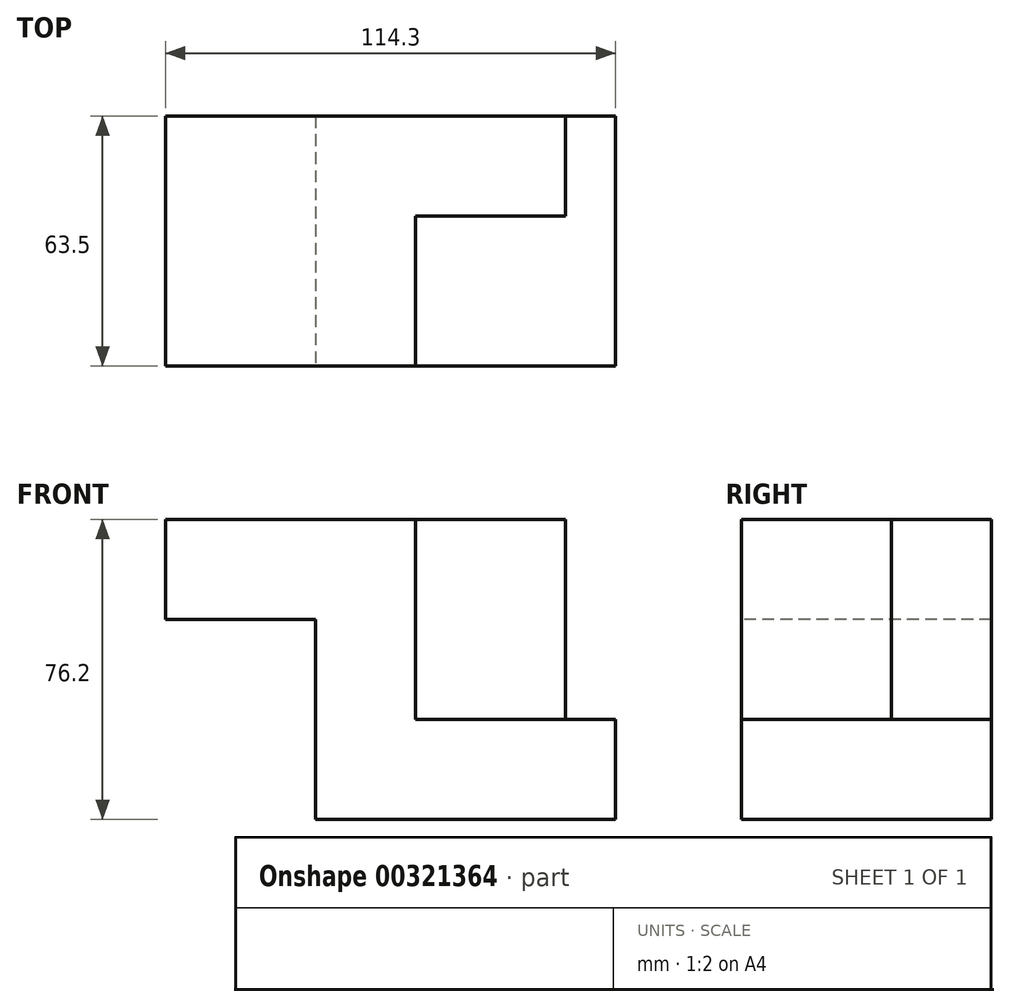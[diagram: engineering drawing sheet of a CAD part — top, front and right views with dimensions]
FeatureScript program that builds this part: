
annotation { "Feature Type Name" : "Feature", "Feature Type Description" : "" }
export const myFeature = defineFeature(function(context is Context, id is Id, definition is map)
    precondition{}
    {
        {
            var Q0;
            Q0=qCreatedBy(makeId("Front.planeOp"),FACE);
            var sketch = newSketch(context, id + "F0", { "sketchPlane" : qUnion([Q0])});
            skLineSegment(sketch, "E0", {"start": v(-34.58, -2.54) * mm, "end": v(-34.58, -27.94) * mm});
            skLineSegment(sketch, "E1", {"start": v(-34.58, -27.94) * mm, "end": v(41.62, -27.94) * mm});
            skLineSegment(sketch, "E2", {"start": v(41.62, -27.94) * mm, "end": v(41.62, -2.54) * mm});
            skLineSegment(sketch, "E3", {"start": v(41.62, -2.54) * mm, "end": v(-34.58, -2.54) * mm});
            skSolve(sketch);
        }
        {
            var Q0;
            Q0 = qSketchRegion(id + "F0", true);
            var Q1;
            Q1=makeQuery(id+"F0.imprint","IMPRINT",FACE,{"disambiguationData":[TD([[makeQuery(id+"F0.imprint","IMPRINT",EDGE,{"derivedFrom":sQuery(id+"F0.wireOp",EDGE,"E0")}),1.0]])]});
            extrude(context, id + "F1", {"entities" : qUnion([Q0, Q1]), "depth" : 63.5 * mm});
        }
        {
            var Q0;
            Q0=makeQuery(id+"F1.opExtrude","SWEPT_FACE",FACE,{"disambiguationData":[OSD([sQuery(id+"F0.wireOp",EDGE,"E3")])]});
            var sketch = newSketch(context, id + "F2", { "sketchPlane" : qUnion([Q0])});
            skLineSegment(sketch, "E4", {"start": v(-9.18, -63.5) * mm, "end": v(-9.18, -25.4) * mm});
            skLineSegment(sketch, "E5", {"start": v(-9.18, -25.4) * mm, "end": v(28.92, -25.4) * mm});
            skLineSegment(sketch, "E6", {"start": v(28.92, -25.4) * mm, "end": v(28.92, 0) * mm});
            skSolve(sketch);
        }
        {
            var Q0;
            {var subQ3=sQuery(id+"F2.wireOp",EDGE,"E4");Q0=makeQuery(id+"F2.imprint","IMPRINT",FACE,{"disambiguationData":[TD([[makeQuery(id+"F2.imprint","IMPRINT",EDGE,{"derivedFrom":subQ3}),1.0]])]});}
            extrude(context, id + "F3", {"entities" : qUnion([Q0]), "operationType" : NewBodyOperationType.ADD, "depth" : 50.8 * mm});
        }
        {
            var Q0;
            {var subQ0=sQuery(id+"F0.wireOp",EDGE,"E0");Q0=makeQuery(id+"F3.boolean.opBoolean","MERGE",FACE,{"derivedFrom":[makeQuery(id+"F1.opExtrude","SWEPT_FACE",FACE,{"disambiguationData":[OSD([subQ0])]}),makeQuery(id+"F3.opExtrude","SWEPT_FACE",FACE,{"disambiguationData":[OSD([subQ0,sQuery(id+"F0.wireOp",EDGE,"E3")])]})]});}
            var sketch = newSketch(context, id + "F4", { "sketchPlane" : qUnion([Q0])});
            skLineSegment(sketch, "E7", {"start": v(0, 22.86) * mm, "end": v(63.5, 22.86) * mm});
            skSolve(sketch);
        }
        {
            var Q0;
            {var subQ0=sQuery(id+"F4.wireOp",EDGE,"E7");Q0=makeQuery(id+"F4.imprint","IMPRINT",FACE,{"disambiguationData":[TD([[makeQuery(id+"F4.imprint","IMPRINT",EDGE,{"derivedFrom":subQ0}),1.0]])]});}
            extrude(context, id + "F5", {"entities" : qUnion([Q0]), "operationType" : NewBodyOperationType.ADD, "depth" : 38.1 * mm});
        }
    });
